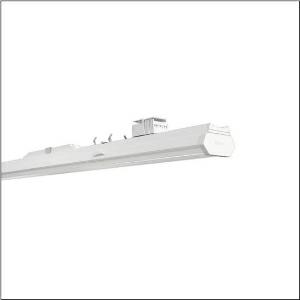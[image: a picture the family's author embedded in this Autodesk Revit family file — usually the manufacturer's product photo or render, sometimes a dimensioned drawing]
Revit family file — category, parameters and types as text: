
# Revit family: licross_r__21_protected_mo_52td12dn48xg_f2a3
name_source: partatom
category: Lighting Fixtures
units: mm (PartAtom-declared; Revit-internal decimal feet)

## family parameters
Cut with Voids When Loaded = No
Host = Face
Light Source = No
Part Type = Normal
Room Calculation Point = No
Round Connector Dimension = Use Diameter
Shared = No

## types (1)
- --- (1 x LED, 8000 lm, 45.3 W, 4000K)
    Apparent Load = 45 VA
    CIE Flux Codes = 73 92 98 99 100
    Color Rendering = 80
    Color Temperature = 4000K
    Default Elevation = 1800 mm
    Description = Licross® 21 Protected MO, luminaire insert, of sheet steel, galvanised, coil coated, white, length: 1.500mm, width: 90mm, height: 103mm, LED rated luminous flux: 8.000lm, light colour: 840, control gear: DALI 2, with plug, 5-pole, with phase selection, mains connection: 220..240V, AC, 50/60Hz, rated input power: 45W, internal wiring halogen-free, primary light control with lens, of plastic, primary optical cover: cover, of PMMA, light emission: direct distribution, primary light characteristic: symmetric, protection rating (complete): IP54, insulation class (complete): insulation class I (protective earthing), certification: CE, ENEC, VDE, UKCA, protection symbol: D if used in an environment with non-conductive dust loads with corresponding accessories, impact resistance: IK06, permissible ambient temperature for indoor applications: -25..+45°C, corresponds to IFS (International Featured Standards) requirements for safety and quality in the food industry, reducing of maximum allowable ambient temperature of 5°C with ceiling mounting, LABS conformity tested according to VDMA 24364:2018-05, packaging unit: 1 piece
    Height = 92 mm
    Lamp = 1 x LED
    Lamp Light Flux = 8000 lm
    Lamp Power = 45.3 W
    Lamp count = 1
    Length = 1500 mm
    Luminous efficacy = 177 lm/W
    Manufacturer = Siteco
    ModVariant = No
    Model = 52TD12DN48XG
    Mounting Place = Ceiling
    Mounting Type = Pendant
    Number of Poles = 1
    OnlyDefault = Yes
    Power Factor = 1
    Product Name = Licross® 21 Protected MO
    Product group = luminaire insert | ceiling pendant
    ProductGroupID = 902
    Protection Class = Protection class I
    Protection Degree = IP 54
    RLX_Detail_Level = 1
    RLX_Emergency_Light_Flux = 0 lm
    RLX_Emergency_Type = 0
    RLX_Emergency_Type_DB = No
    RlxData = <blob elided: 24341 chars, md5=9cdad899>
    Socket = socket
    Standby Power = 0 W
    System Light Flux = 8000 lm
    System Power = 45 W
    Type Comments = factory setting: luminous flux: 100 % | dim-lin: 254 | 305 mA
    Type Image = l_1256148.jpg
    URL = http://relux.com
    VarID = @adj_150241
    Voltage = 0 V
    Weight = 0.00 kg
    Width = 88 mm

## geometry (parser evidence)
native form markers: Blend x4, Sweep x10
no freeform markers — native parametric forms only
